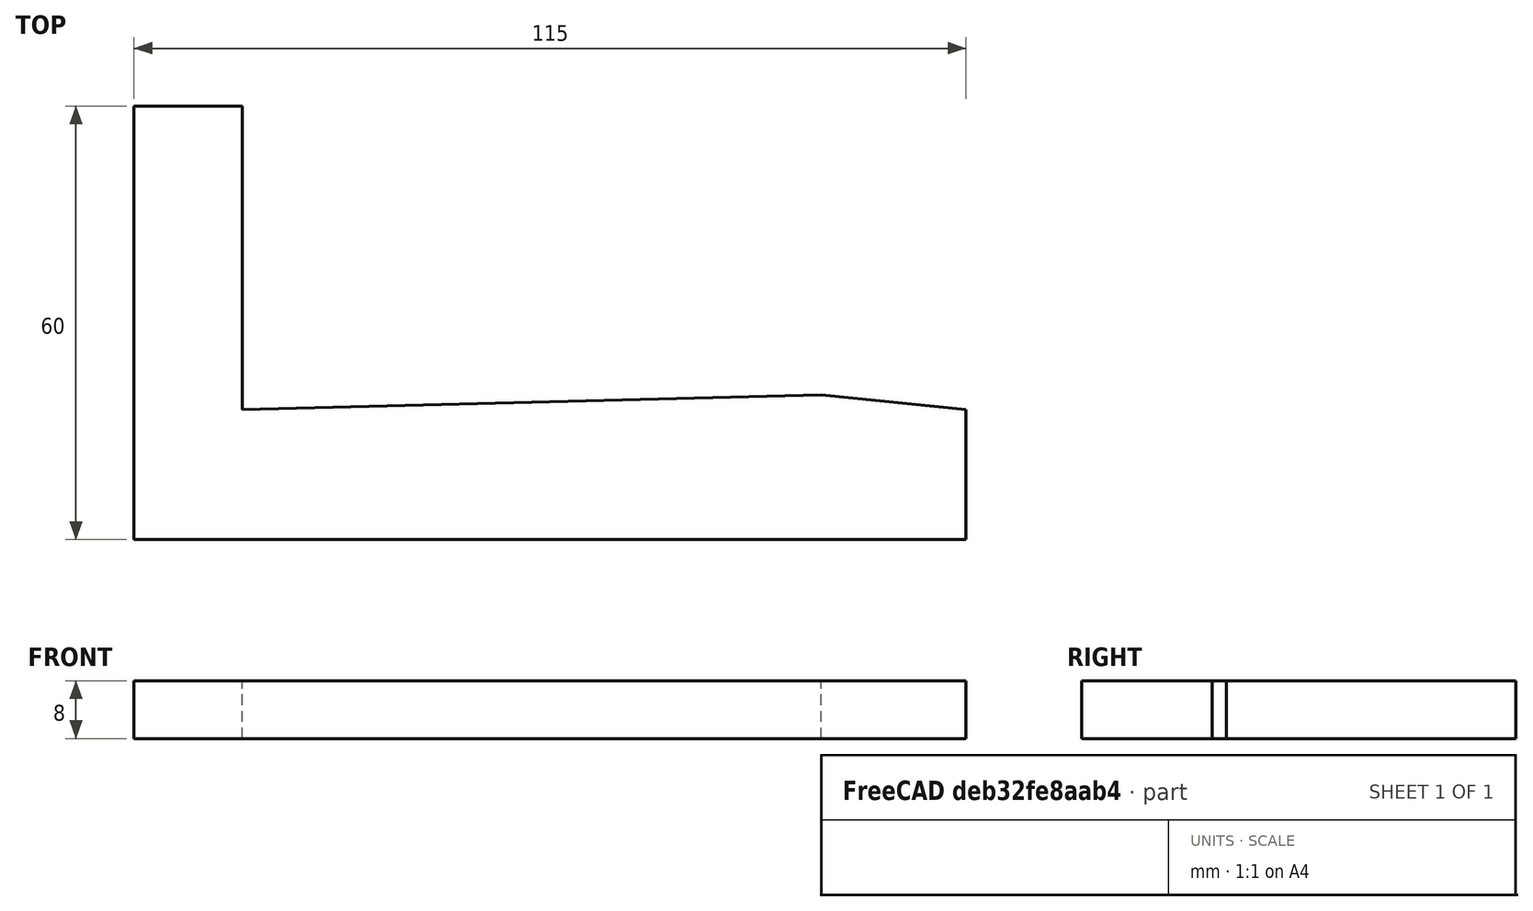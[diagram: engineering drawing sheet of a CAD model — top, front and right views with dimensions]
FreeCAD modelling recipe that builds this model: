
FCSTD DOCUMENT  (FreeCAD 0.19R)
Label: DoorTool
License: All rights reserved
LicenseURL: http://en.wikipedia.org/wiki/All_rights_reserved
objects: Sketcher::SketchObject×1, PartDesign::Pad×1, PartDesign::Body×1, Mesh::Feature×1
note: 4 computed .brp shape members not serialized (recipe doc carries the construction recipe); baked Part::Feature solids carry a one-line shape summary decoded from their .brp

FEATURE [Sketcher::SketchObject] Sketch
  FullyConstrained = true
  MapMode = 5
  Support = -> [XY_Plane]
  sketch-geometry (7):
    g0: LineSegment StartX=0 StartY=0 StartZ=0 EndX=0 EndY=18 EndZ=0
    g1: LineSegment StartX=0 StartY=18 StartZ=0 EndX=-20 EndY=20 EndZ=0
    g2: LineSegment StartX=-20 StartY=20 StartZ=0 EndX=-100 EndY=18 EndZ=0
    g3: LineSegment StartX=-100 StartY=18 StartZ=0 EndX=-100 EndY=60 EndZ=0
    g4: LineSegment StartX=-100 StartY=60 StartZ=0 EndX=-115 EndY=60 EndZ=0
    g5: LineSegment StartX=-115 StartY=60 StartZ=0 EndX=-115 EndY=0 EndZ=0
    g6: LineSegment StartX=-115 StartY=0 StartZ=0 EndX=0 EndY=0 EndZ=0
  constraints (20):
    c: Coincident(g-1,g0)
    c: PointOnObject(g0,g-2)
    c: Coincident(g0,g1)
    c: Coincident(g1,g2)
    c: Coincident(g2,g3)
    c: Vertical(g3)
    c: Coincident(g3,g4)
    c: Horizontal(g4)
    c: Coincident(g4,g5)
    c: PointOnObject(g5,g-1)
    c: Coincident(g5,g6)
    c: Coincident(g6,g0)
    c: DistanceY(g0,g0) = 18
    c: DistanceY(g1) = 20
    c: DistanceY(g2) = 18
    c: DistanceX(g2) = -100
    c: DistanceX(g1) = -20
    c: Vertical(g5)
    c: DistanceY(g4) = 60
    c: DistanceX(g4,g4) = 15
FEATURE [PartDesign::Pad] Pad
  Direction = (1,1,1)
  Length = 8
  Length2 = 100
  Profile = -> Sketch
  Type = 0
FEATURE [PartDesign::Body] Body
  Group = -> [Sketch,Pad]
  Origin = -> Origin
  Tip = -> Pad
FEATURE [Mesh::Feature] Mesh  label="Pad (Meshed)"
